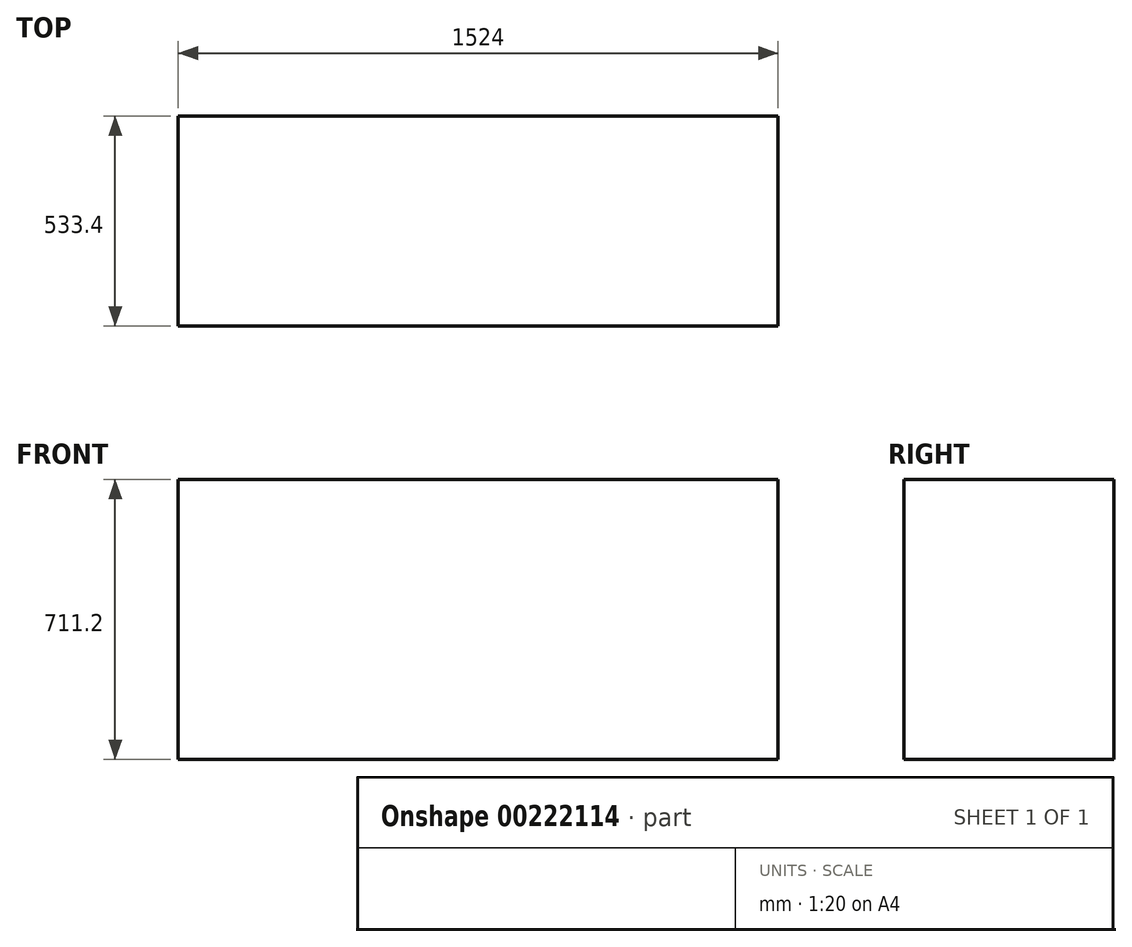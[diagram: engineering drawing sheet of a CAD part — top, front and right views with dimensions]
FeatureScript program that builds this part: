
annotation { "Feature Type Name" : "Feature", "Feature Type Description" : "" }
export const myFeature = defineFeature(function(context is Context, id is Id, definition is map)
    precondition{}
    {
        {
            var Q0;
            Q0=qCreatedBy(makeId("Top.planeOp"),FACE);
            var sketch = newSketch(context, id + "F0", { "sketchPlane" : qUnion([Q0])});
            skLineSegment(sketch, "E0.bottom", {"start": v(0, 0) * mm, "end": v(1524, 0) * mm});
            skLineSegment(sketch, "E0.top", {"start": v(0, 533.4) * mm, "end": v(1524, 533.4) * mm});
            skLineSegment(sketch, "E0.left", {"start": v(0, 0) * mm, "end": v(0, 533.4) * mm});
            skLineSegment(sketch, "E0.right", {"start": v(1524, 0) * mm, "end": v(1524, 533.4) * mm});
            skSolve(sketch);
        }
        {
            var Q0;
            Q0=makeQuery(id+"F0.imprint","IMPRINT",FACE,{"disambiguationData":[TD([[makeQuery(id+"F0.imprint","IMPRINT",EDGE,{"derivedFrom":sQuery(id+"F0.wireOp",EDGE,"E0.bottom")}),1.0]])]});
            extrude(context, id + "F1", {"entities" : qUnion([Q0]), "depth" : 711.2 * mm});
        }
    });
